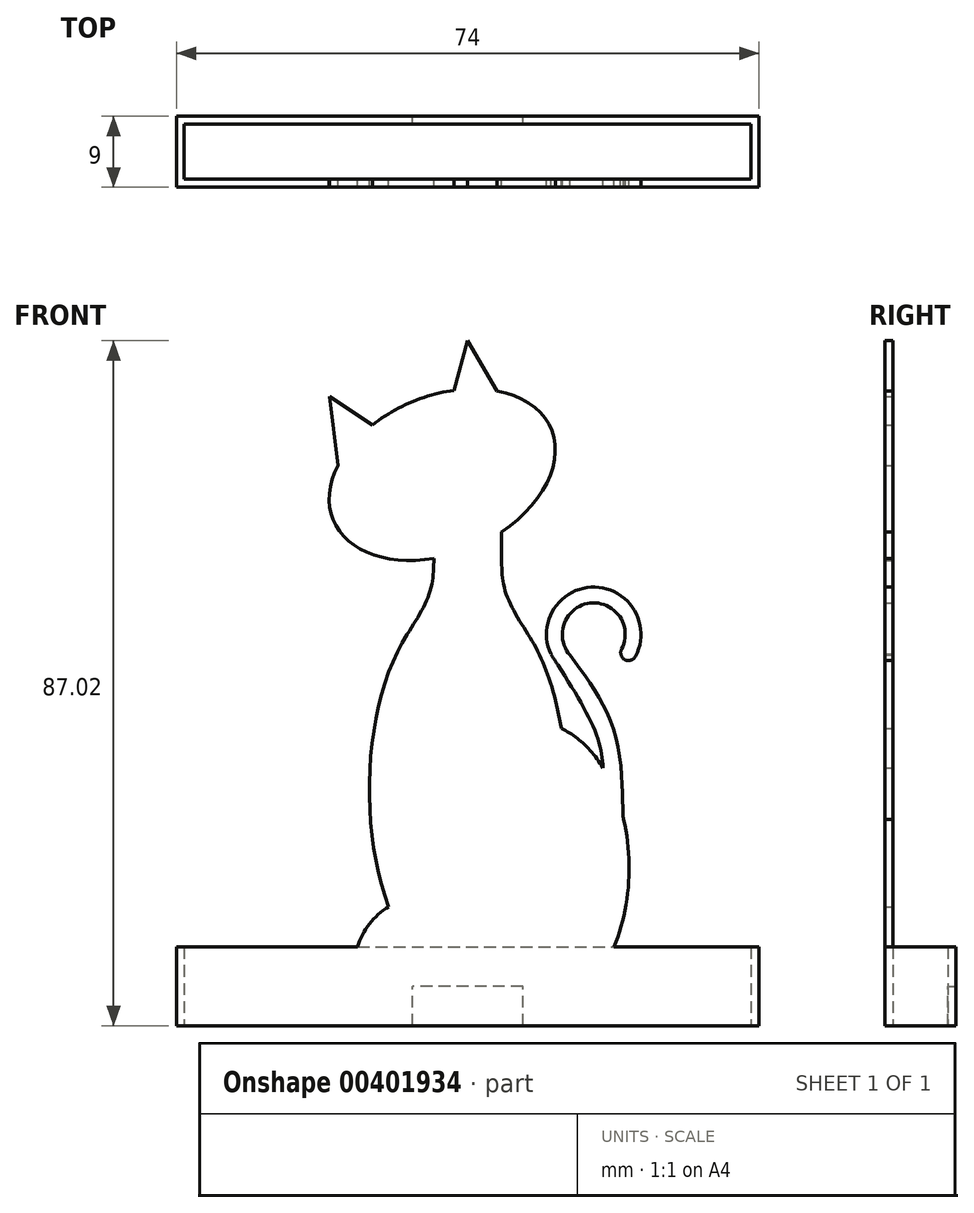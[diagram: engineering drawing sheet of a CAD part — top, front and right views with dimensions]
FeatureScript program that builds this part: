
annotation { "Feature Type Name" : "Feature", "Feature Type Description" : "" }
export const myFeature = defineFeature(function(context is Context, id is Id, definition is map)
    precondition{}
    {
        {
            var Q0;
            Q0=qCreatedBy(makeId("Front.planeOp"),FACE);
            var sketch = newSketch(context, id + "F0", { "sketchPlane" : qUnion([Q0])});
            skLineSegment(sketch, "E0", {"start": v(-37, 10) * mm, "end": v(37, 10) * mm});
            skEllipticalArc(sketch, "E1", {});
            skEllipticalArc(sketch, "E2", {});
            skPoint(sketch, "E3.1.internal.snap0", {"position": v(0, 55) * mm});
            skFitSpline(sketch, "E3", {"points": [v(-7.69, 49.71) * mm, v(-4.84, 55) * mm, v(-4.29, 59.36) * mm], "startDerivative": vector(6.36, 9.93) * mm, "endDerivative": vector(0.24, 9.4) * mm});
            skFitSpline(sketch, "E4.MirrorCS", {"points": [v(7.69, 49.71) * mm, v(4.84, 55) * mm, v(4.29, 59.36) * mm], "startDerivative": vector(-6.36, 9.93) * mm, "endDerivative": vector(-0.24, 9.4) * mm});
            skLineSegment(sketch, "E5", {"start": v(4.29, 59.36) * mm, "end": v(4.29, 62.74) * mm});
            skLineSegment(sketch, "E6", {"start": v(-16.5, 71.15) * mm, "end": v(-17.58, 79.94) * mm});
            skLineSegment(sketch, "E7", {"start": v(-17.58, 79.94) * mm, "end": v(-12.1, 76.3) * mm});
            skLineSegment(sketch, "E8", {"start": v(-1.72, 80.72) * mm, "end": v(0, 87.02) * mm});
            skLineSegment(sketch, "E9", {"start": v(0, 87.02) * mm, "end": v(3.73, 80.64) * mm});
            skEllipticalArc(sketch, "E10", {});
            skArc(sketch, "E11", {"start": v(-10.04, 15.1) * mm, "mid": v(-12.49, 12.92) * mm, "end": v(-13.98, 10) * mm});
            skPoint(sketch, "E12.startSnap0", {"position": v(20.5, 20) * mm});
            skArc(sketch, "E13", {"start": v(19.55, 47.85) * mm, "mid": v(15.54, 53.69) * mm, "end": v(13, 47.08) * mm});
            skArc(sketch, "E14", {"start": v(21.32, 46.92) * mm, "mid": v(15.35, 55.68) * mm, "end": v(11.45, 45.82) * mm});
            skFitSpline(sketch, "E15", {"points": [v(13, 47.08) * mm, v(18.98, 35.93) * mm, v(19.75, 26.42) * mm, v(19.8, 26.23) * mm], "startDerivative": vector(14.66, -19.96) * mm, "endDerivative": vector(-0.2, -1.9) * mm});
            skFitSpline(sketch, "E16", {"points": [v(10.57, 47.19) * mm, v(14.99, 39.92) * mm, v(16.8, 35.55) * mm, v(17.2, 32.74) * mm], "startDerivative": vector(11.35, -17.68) * mm, "endDerivative": vector(0.9, -10.93) * mm});
            skArc(sketch, "E17", {"start": v(19.55, 47.85) * mm, "mid": v(19.97, 46.5) * mm, "end": v(21.32, 46.92) * mm});
            skPoint(sketch, "E18.start.orphan", {"position": v(12.01, 49.71) * mm});
            skLineSegment(sketch, "E19", {"start": v(-13.98, 10) * mm, "end": v(-7.5, 10) * mm});
            skEllipticalArc(sketch, "E20.trimOffspring", {});
            skEllipticalArc(sketch, "E21.trimOffspring", {});
            skEllipticalArc(sketch, "E22.trimOffspring", {});
            skEllipticalArc(sketch, "E23.trimOffspring", {});
            skPoint(sketch, "E24.end.orphan", {"position": v(-45.84, 70) * mm});
            skPoint(sketch, "E24.start.orphan", {"position": v(-45.84, 80) * mm});
            skPoint(sketch, "E25.start.orphan", {"position": v(-61.86, 80) * mm});
            skPoint(sketch, "E26.end.orphan", {"position": v(-55.67, 30) * mm});
            skPoint(sketch, "E26.start.orphan", {"position": v(-55.67, 10) * mm});
            skPoint(sketch, "E27.end.orphan", {"position": v(-37, -12.95) * mm});
            skPoint(sketch, "E27.start.orphan", {"position": v(0, -12.95) * mm});
            skPoint(sketch, "E28.end.orphan", {"position": v(-61.86, 10) * mm});
            skPoint(sketch, "E28.start.orphan", {"position": v(-61.86, 0) * mm});
            const initialGuessF0  = {"E1": [0, 0.03, 0, -1, 0.025, 0.0125, 1.8853250248222464, 2.4791891291728323], "E2": [-0.003240203717723489, 0.07, -0.9218436140569326, -0.3875620611237034, 0.015, 0.01, 1.8494400704554055, 3.932115541175288], "E10": [0.008567341603337796, 0.02, 0, 1, 0.01846289216664839, 0.011933219928808062, 5.474108614984713, 6.001299254167671], "E20.trimOffspring": [0, 0.03, 0, -1, 0.025, 0.0125, 3.803996178006752, 5.350424236796998], "E21.trimOffspring": [0.008567341603337796, 0.02, 0, 1, 0.01846289216664839, 0.011933219928808062, 4.140017654164218, 5.056663556909229], "E22.trimOffspring": [-0.003240203717723489, 0.07, -0.9218436140569326, -0.3875620611237034, 0.015, 0.01, 5.614738392914379, 1.2244114026619095], "E23.trimOffspring": [-0.003240203717723489, 0.07, -0.9218436140569326, -0.3875620611237034, 0.015, 0.01, 4.333269339782975, 5.103753518535238]};
            skSetInitialGuess(sketch, initialGuessF0);
            skSolve(sketch);
        }
        {
            var Q0;
            Q0=makeQuery(id+"F0.imprint","IMPRINT",FACE,{"disambiguationData":[TD([[makeQuery(id+"F0.imprint","IMPRINT",EDGE,{"derivedFrom":sQuery(id+"F0.wireOp",EDGE,"E1")}),1.0]])]});
            extrude(context, id + "F1", {"entities" : qUnion([Q0]), "depth" : 1 * mm});
        }
        {
            var Q0;
            Q0=makeQuery(id+"F1.opExtrude","CAP_FACE",FACE,{"disambiguationData":[OSD([sQuery(id+"F0.wireOp",EDGE,"E0"),sQuery(id+"F0.wireOp",EDGE,"E1"),sQuery(id+"F0.wireOp",EDGE,"E2"),sQuery(id+"F0.wireOp",EDGE,"E3"),sQuery(id+"F0.wireOp",EDGE,"E4.MirrorCS"),sQuery(id+"F0.wireOp",EDGE,"E5"),sQuery(id+"F0.wireOp",EDGE,"E6"),sQuery(id+"F0.wireOp",EDGE,"E7"),sQuery(id+"F0.wireOp",EDGE,"E8"),sQuery(id+"F0.wireOp",EDGE,"E9"),sQuery(id+"F0.wireOp",EDGE,"E10"),sQuery(id+"F0.wireOp",EDGE,"E11"),sQuery(id+"F0.wireOp",EDGE,"E13"),sQuery(id+"F0.wireOp",EDGE,"E14"),sQuery(id+"F0.wireOp",EDGE,"E15"),sQuery(id+"F0.wireOp",EDGE,"E16"),sQuery(id+"F0.wireOp",EDGE,"E17"),sQuery(id+"F0.wireOp",EDGE,"E19"),sQuery(id+"F0.wireOp",EDGE,"E20.trimOffspring"),sQuery(id+"F0.wireOp",EDGE,"E21.trimOffspring"),sQuery(id+"F0.wireOp",EDGE,"E22.trimOffspring"),sQuery(id+"F0.wireOp",EDGE,"E23.trimOffspring")])],"isStart":false});
            var sketch = newSketch(context, id + "F2", { "sketchPlane" : qUnion([Q0])});
            skLineSegment(sketch, "E29.bottom", {"start": v(-37, 0) * mm, "end": v(37, 0) * mm});
            skLineSegment(sketch, "E29.top", {"start": v(-37, 10) * mm, "end": v(37, 10) * mm});
            skLineSegment(sketch, "E29.left", {"start": v(-37, 0) * mm, "end": v(-37, 10) * mm});
            skLineSegment(sketch, "E29.right", {"start": v(37, 0) * mm, "end": v(37, 10) * mm});
            skSolve(sketch);
        }
        {
            var Q0;
            Q0=makeQuery(id+"F2.imprint","IMPRINT",FACE,{"disambiguationData":[TD([[makeQuery(id+"F2.imprint","IMPRINT",EDGE,{"derivedFrom":sQuery(id+"F2.wireOp",EDGE,"E29.bottom")}),1.0]])]});
            extrude(context, id + "F3", {"entities" : qUnion([Q0]), "operationType" : NewBodyOperationType.ADD, "oppositeDirection" : true, "depth" : 9 * mm});
        }
        {
            var Q0;
            Q0=makeQuery(id+"F3.opExtrude","SWEPT_FACE",FACE,{"disambiguationData":[OSD([sQuery(id+"F2.wireOp",EDGE,"E29.bottom")])]});
            var sketch = newSketch(context, id + "F4", { "sketchPlane" : qUnion([Q0])});
            skPoint(sketch, "E30.startSnap0", {"position": v(0, 1) * mm});
            skLineSegment(sketch, "E31.bottom", {"start": v(-36, 0) * mm, "end": v(36, 0) * mm});
            skLineSegment(sketch, "E31.top", {"start": v(-36, -7) * mm, "end": v(36, -7) * mm});
            skLineSegment(sketch, "E31.left", {"start": v(-36, 0) * mm, "end": v(-36, -7) * mm});
            skLineSegment(sketch, "E31.right", {"start": v(36, 0) * mm, "end": v(36, -7) * mm});
            skSolve(sketch);
        }
        {
            var Q0;
            Q0=makeQuery(id+"F4.imprint","IMPRINT",FACE,{"disambiguationData":[TD([[makeQuery(id+"F4.imprint","IMPRINT",EDGE,{"derivedFrom":sQuery(id+"F4.wireOp",EDGE,"E31.bottom")}),-1.0]])]});
            extrude(context, id + "F5", {"entities" : qUnion([Q0]), "operationType" : NewBodyOperationType.REMOVE, "oppositeDirection" : true, "depth" : 15 * mm});
        }
        {
            var Q0;
            Q0=makeQuery(id+"F3.opExtrude","CAP_FACE",FACE,{"disambiguationData":[OSD([sQuery(id+"F2.wireOp",EDGE,"E29.bottom"),sQuery(id+"F2.wireOp",EDGE,"E29.top"),sQuery(id+"F2.wireOp",EDGE,"E29.left"),sQuery(id+"F2.wireOp",EDGE,"E29.right")])],"isStart":false});
            var sketch = newSketch(context, id + "F6", { "sketchPlane" : qUnion([Q0])});
            skLineSegment(sketch, "E32.bottom", {"start": v(-7, 0) * mm, "end": v(7, 0) * mm});
            skLineSegment(sketch, "E32.top", {"start": v(-7, 5) * mm, "end": v(7, 5) * mm});
            skLineSegment(sketch, "E32.left", {"start": v(-7, 0) * mm, "end": v(-7, 5) * mm});
            skLineSegment(sketch, "E32.right", {"start": v(7, 0) * mm, "end": v(7, 5) * mm});
            skSolve(sketch);
        }
        {
            var Q0;
            Q0=makeQuery(id+"F6.imprint","IMPRINT",FACE,{"disambiguationData":[TD([[makeQuery(id+"F6.imprint","IMPRINT",EDGE,{"derivedFrom":sQuery(id+"F6.wireOp",EDGE,"E32.bottom")}),-1.0]])]});
            extrude(context, id + "F7", {"entities" : qUnion([Q0]), "operationType" : NewBodyOperationType.REMOVE, "oppositeDirection" : true, "depth" : 3 * mm});
        }
    });
